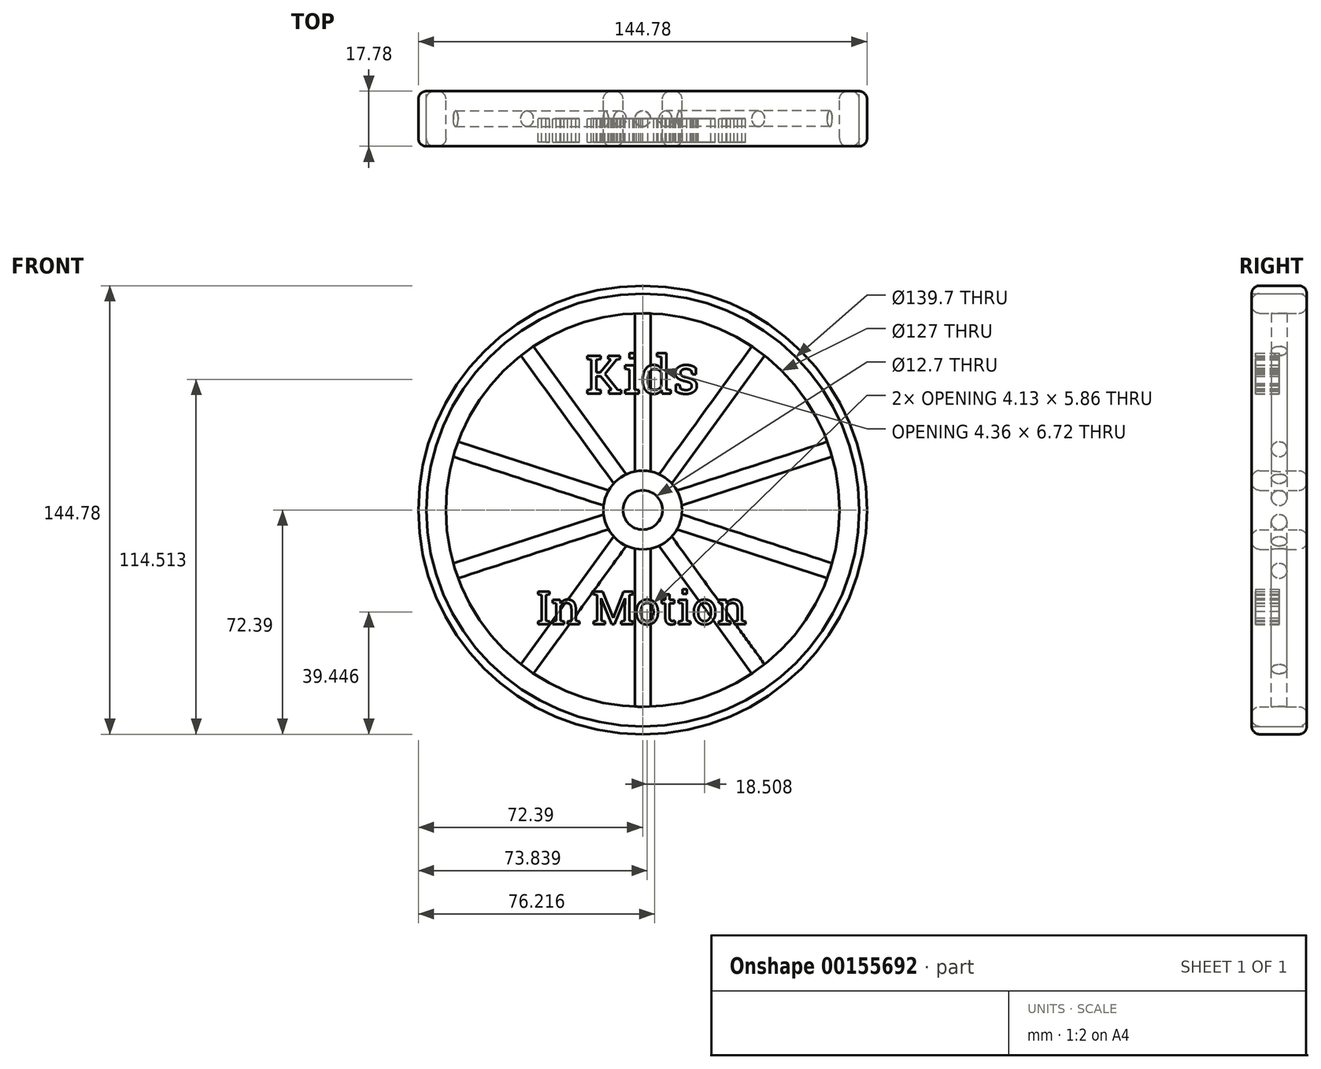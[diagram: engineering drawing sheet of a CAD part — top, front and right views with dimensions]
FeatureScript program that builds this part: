
annotation { "Feature Type Name" : "Feature", "Feature Type Description" : "" }
export const myFeature = defineFeature(function(context is Context, id is Id, definition is map)
    precondition{}
    {
        {
            var Q0;
            Q0=qCreatedBy(makeId("Front.planeOp"),FACE);
            var sketch = newSketch(context, id + "F0", { "sketchPlane" : qUnion([Q0])});
            skCircle(sketch, "E0", {"center": v(0, 0) * mm, "radius": 63.5 * mm});
            skCircle(sketch, "E1.0", {"center": v(0, 0) * mm, "radius": 69.85 * mm});
            skCircle(sketch, "E2", {"center": v(0, 0) * mm, "radius": 12.7 * mm});
            skCircle(sketch, "E3", {"center": v(0, 0) * mm, "radius": 6.35 * mm});
            skLineSegment(sketch, "E4", {"start": v(-2.54, 63.45) * mm, "end": v(-2.54, 12.44) * mm});
            skLineSegment(sketch, "E5", {"start": v(2.54, 12.44) * mm, "end": v(2.54, 63.45) * mm});
            skCircle(sketch, "E6.0", {"center": v(0, 0) * mm, "radius": 72.39 * mm});
            skSolve(sketch);
        }
        {
            var Q0;
            Q0=makeQuery(id+"F0.imprint","IMPRINT",FACE,{"disambiguationData":[TD([[makeQuery(id+"F0.imprint","IMPRINT",EDGE,{"derivedFrom":sQuery(id+"F0.wireOp",EDGE,"E3")}),-1.0]])]});
            var Q1;
            Q1=makeQuery(id+"F0.imprint","IMPRINT",FACE,{"disambiguationData":[TD([[makeQuery(id+"F0.imprint","IMPRINT",EDGE,{"derivedFrom":sQuery(id+"F0.wireOp",EDGE,"E1.0")}),1.0]])]});
            extrude(context, id + "F1", {"entities" : qUnion([Q0, Q1]), "endBound" : BoundingType.SYMMETRIC, "depth" : 17.78 * mm, "offsetDistance" : 25.4 * mm});
        }
        {
            var Q0;
            {var subQ0=sQuery(id+"F0.wireOp",EDGE,"E4");Q0=makeQuery(id+"F0.imprint","IMPRINT",FACE,{"disambiguationData":[TD([[makeQuery(id+"F0.imprint","IMPRINT",EDGE,{"derivedFrom":subQ0}),1.0]])]});}
            extrude(context, id + "F2", {"entities" : qUnion([Q0]), "operationType" : NewBodyOperationType.ADD, "endBound" : BoundingType.SYMMETRIC, "depth" : 5.08 * mm, "offsetDistance" : 25.4 * mm});
        }
        {
            var Q0;
            Q0=makeQuery(id+"F2.opExtrude","CAP_EDGE",EDGE,{"disambiguationData":[OSD([sQuery(id+"F0.wireOp",EDGE,"E5")])],"isStart":false});
            var Q1;
            Q1=makeQuery(id+"F2.opExtrude","CAP_EDGE",EDGE,{"disambiguationData":[OSD([sQuery(id+"F0.wireOp",EDGE,"E5")])],"isStart":true});
            var Q2;
            Q2=makeQuery(id+"F2.opExtrude","CAP_EDGE",EDGE,{"disambiguationData":[OSD([sQuery(id+"F0.wireOp",EDGE,"E4")])],"isStart":false});
            var Q3;
            Q3=makeQuery(id+"F2.opExtrude","CAP_EDGE",EDGE,{"disambiguationData":[OSD([sQuery(id+"F0.wireOp",EDGE,"E4")])],"isStart":true});
            fillet(context, id + "F3", {"entities" : qUnion([Q0, Q1, Q2, Q3]), "radius" : 2.54 * mm, "tangentPropagation" : true, "allowEdgeOverflow" : false});
        }
        {
            var Q0;
            Q0=makeQuery(id+"F1.opExtrude","SWEPT_BODY",BODY,{"disambiguationData":[OSD([sQuery(id+"F0.wireOp",EDGE,"E0"),sQuery(id+"F0.wireOp",EDGE,"E1.0")])]});
            var Q1;
            Q1=sQuery(id+"F0.wireOp",EDGE,"E3");
            circularPattern(context, id + "F4", {"operationType" : NewBodyOperationType.ADD, "entities" : qUnion([Q0]), "axis" : qUnion([Q1]), "angle" : 360 * degree, "instanceCount" : 10, "equalSpace" : true});
        }
        {
            var Q0;
            Q0=makeQuery(id+"F0.imprint","IMPRINT",FACE,{"disambiguationData":[TD([[makeQuery(id+"F0.imprint","IMPRINT",EDGE,{"derivedFrom":sQuery(id+"F0.wireOp",EDGE,"E1.0")}),-1.0]])]});
            extrude(context, id + "F5", {"entities" : qUnion([Q0]), "endBound" : BoundingType.SYMMETRIC, "depth" : 17.78 * mm, "offsetDistance" : 25.4 * mm});
        }
        {
            var Q0;
            Q0=makeQuery(id+"F5.opExtrude","SWEPT_FACE",FACE,{"disambiguationData":[OSD([sQuery(id+"F0.wireOp",EDGE,"E6.0")])]});
            fillet(context, id + "F6", {"entities" : qUnion([Q0]), "radius" : 2.54 * mm, "tangentPropagation" : true, "allowEdgeOverflow" : false});
        }
        {
            var Q0;
            Q0=makeQuery(id+"F1.opExtrude","CAP_FACE",FACE,{"disambiguationData":[OSD([sQuery(id+"F0.wireOp",EDGE,"E2"),sQuery(id+"F0.wireOp",EDGE,"E3")])],"isStart":false});
            var Q1;
            Q1=makeQuery(id+"F1.opExtrude","CAP_FACE",FACE,{"disambiguationData":[OSD([sQuery(id+"F0.wireOp",EDGE,"E2"),sQuery(id+"F0.wireOp",EDGE,"E3")])],"isStart":true});
            var Q2;
            Q2=makeQuery(id+"F1.opExtrude","CAP_FACE",FACE,{"disambiguationData":[OSD([sQuery(id+"F0.wireOp",EDGE,"E0"),sQuery(id+"F0.wireOp",EDGE,"E1.0")])],"isStart":false});
            var Q3;
            Q3=makeQuery(id+"F1.opExtrude","CAP_FACE",FACE,{"disambiguationData":[OSD([sQuery(id+"F0.wireOp",EDGE,"E0"),sQuery(id+"F0.wireOp",EDGE,"E1.0")])],"isStart":true});
            fillet(context, id + "F7", {"entities" : qUnion([Q0, Q1, Q2, Q3]), "radius" : 2.54 * mm, "tangentPropagation" : true, "allowEdgeOverflow" : false});
        }
        {
            var Q0;
            Q0=qCreatedBy(makeId("Front.planeOp"),FACE);
            var sketch = newSketch(context, id + "F8", { "sketchPlane" : qUnion([Q0])});
            skText(sketch, "E7", { "text": "Kids\n", "fontName": "RobotoSlab-Regular.ttf"});
            skText(sketch, "E8", { "text": "In Motion\n", "fontName": "RobotoSlab-Regular.ttf"});
            const initialGuessF8  = {"E7": [-0.01854, 0.0376, 1, 0, 0.01234], "E8": [-0.0343, -0.03683, 1, 0, 0.01061]};
            skSetInitialGuess(sketch, initialGuessF8);
            skSolve(sketch);
        }
        {
            var Q0;
            Q0 = qSketchRegion(id + "F8", true);
            extrude(context, id + "F9", {"entities" : qUnion([Q0]), "depth" : 7.62 * mm, "offsetDistance" : 25.4 * mm});
        }
    });
